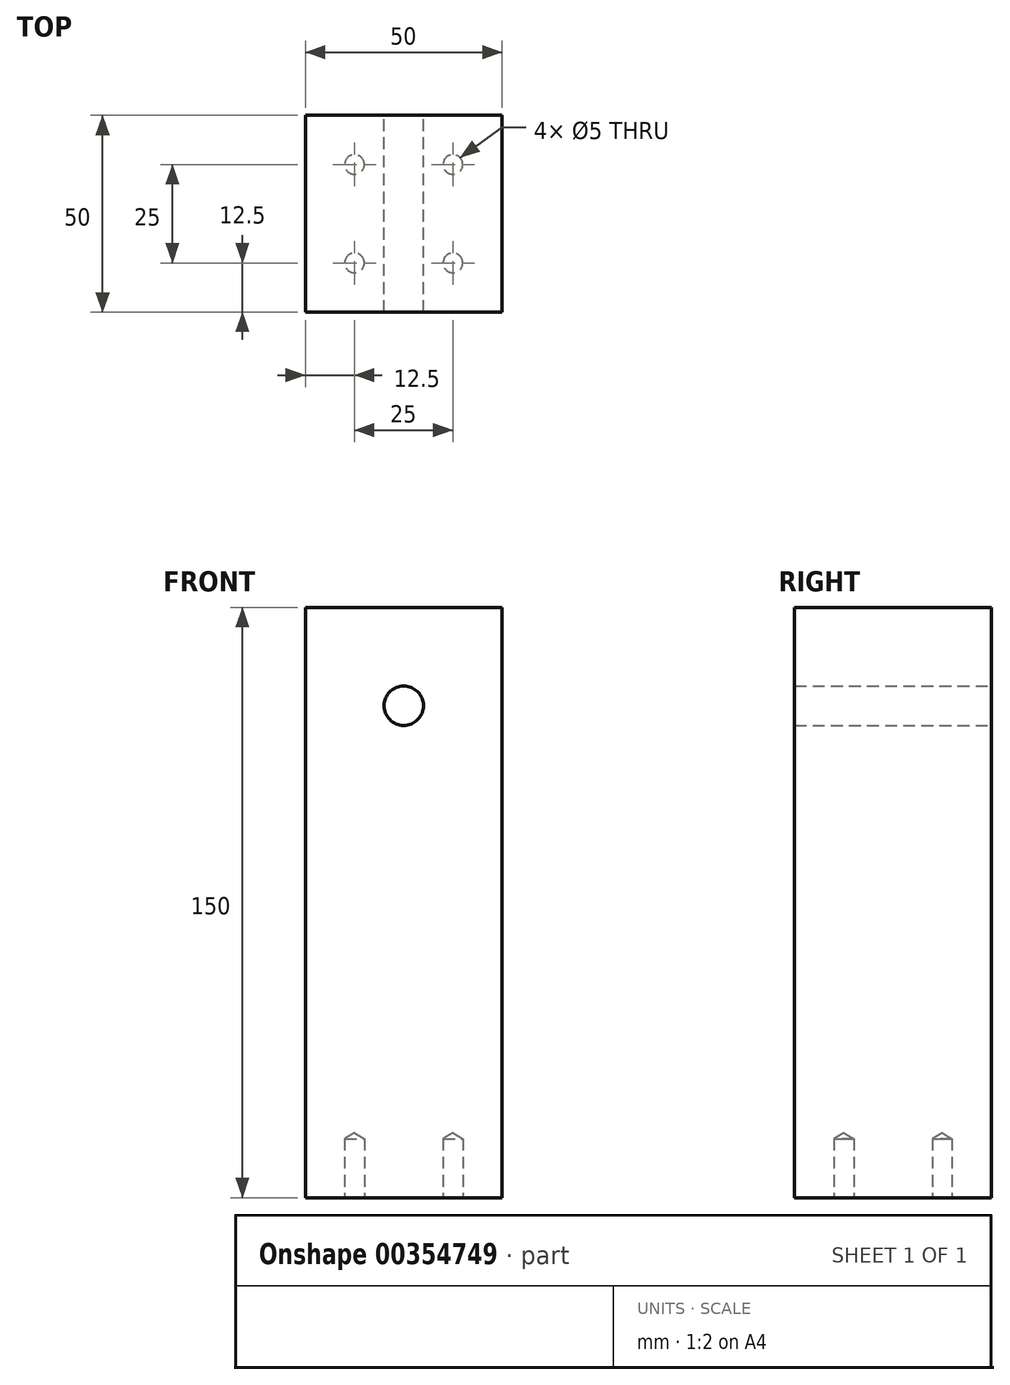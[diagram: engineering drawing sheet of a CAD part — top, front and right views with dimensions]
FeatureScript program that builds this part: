
annotation { "Feature Type Name" : "Feature", "Feature Type Description" : "" }
export const myFeature = defineFeature(function(context is Context, id is Id, definition is map)
    precondition{}
    {
        {
            var Q0;
            Q0=qCreatedBy(makeId("Front.planeOp"),FACE);
            var sketch = newSketch(context, id + "F0", { "sketchPlane" : qUnion([Q0])});
            skLineSegment(sketch, "E0.bottom", {"start": v(25, 75) * mm, "end": v(-25, 75) * mm});
            skLineSegment(sketch, "E0.top", {"start": v(25, -75) * mm, "end": v(-25, -75) * mm});
            skLineSegment(sketch, "E0.left", {"start": v(25, 75) * mm, "end": v(25, -75) * mm});
            skLineSegment(sketch, "E0.right", {"start": v(-25, 75) * mm, "end": v(-25, -75) * mm});
            skPoint(sketch, "E0.middle", {"position": v(0, 0) * mm});
            skPoint(sketch, "E1.endSnap0", {"position": v(0, 75) * mm});
            skCircle(sketch, "E2", {"center": v(0, 50) * mm, "radius": 5 * mm});
            skSolve(sketch);
        }
        {
            var Q0;
            Q0 = qSketchRegion(id + "F0", true);
            extrude(context, id + "F1", {"entities" : qUnion([Q0]), "depth" : 50 * mm});
        }
        {
            var Q0;
            Q0=makeQuery(id+"F1.opExtrude","SWEPT_FACE",FACE,{"disambiguationData":[OSD([sQuery(id+"F0.wireOp",EDGE,"E0.top")])]});
            var sketch = newSketch(context, id + "F2", { "sketchPlane" : qUnion([Q0])});
            skPoint(sketch, "E3.middle", {"position": v(0, 25) * mm});
            skPoint(sketch, "E3.middle.positionSnap0", {"position": v(25, 25) * mm});
            skPoint(sketch, "E3.centerSnap0", {"position": v(25, 25) * mm});
            skCircle(sketch, "E4", {"center": v(-12.5, 37.5) * mm, "radius": 2.5 * mm});
            skCircle(sketch, "E5", {"center": v(12.5, 37.5) * mm, "radius": 2.5 * mm});
            skCircle(sketch, "E6", {"center": v(12.5, 12.5) * mm, "radius": 2.5 * mm});
            skCircle(sketch, "E7", {"center": v(-12.5, 12.5) * mm, "radius": 2.5 * mm});
            skSolve(sketch);
        }
        {
            var Q0;
            Q0=sQuery(id+"F2.wireOp",VERTEX,"E5.center");
            var Q1;
            Q1=sQuery(id+"F2.wireOp",VERTEX,"E6.center");
            var Q2;
            Q2=sQuery(id+"F2.wireOp",VERTEX,"E7.center");
            var Q3;
            Q3=sQuery(id+"F2.wireOp",VERTEX,"E4.center");
            var Q4;
            Q4=makeQuery(id+"F1.opExtrude","SWEPT_BODY",BODY,{"disambiguationData":[OSD([sQuery(id+"F0.wireOp",EDGE,"E0.bottom"),sQuery(id+"F0.wireOp",EDGE,"E0.top"),sQuery(id+"F0.wireOp",EDGE,"E0.left"),sQuery(id+"F0.wireOp",EDGE,"E0.right"),sQuery(id+"F0.wireOp",EDGE,"E2")])]});
            hole(context, id + "F3", {"style" : HoleStyle.SIMPLE, "endStyle" : HoleEndStyle.BLIND, "standardTappedOrClearance" : lookupTablePath({ "standard" : "ISO", "engagement" : "75%", "pitch" : "1 mm", "size" : "M6", "type" : "Tapped" }), "standardBlindInLast" : lookupTablePath({ "standard" : "ISO", "engagement" : "75%", "pitch" : "1 mm", "size" : "M6", "type" : "Tapped" }), "holeDiameter" : 5 * mm, "showTappedDepth" : true, "holeDepth" : 15 * mm, "isTappedThrough" : true, "tappedDepth" : 12 * mm, "tapClearance" : 3, "startFromSketch" : true, "locations" : qUnion([Q0, Q1, Q2, Q3]), "scope" : qUnion([Q4]), "majorDiameter" : 6 * mm});
        }
    });
